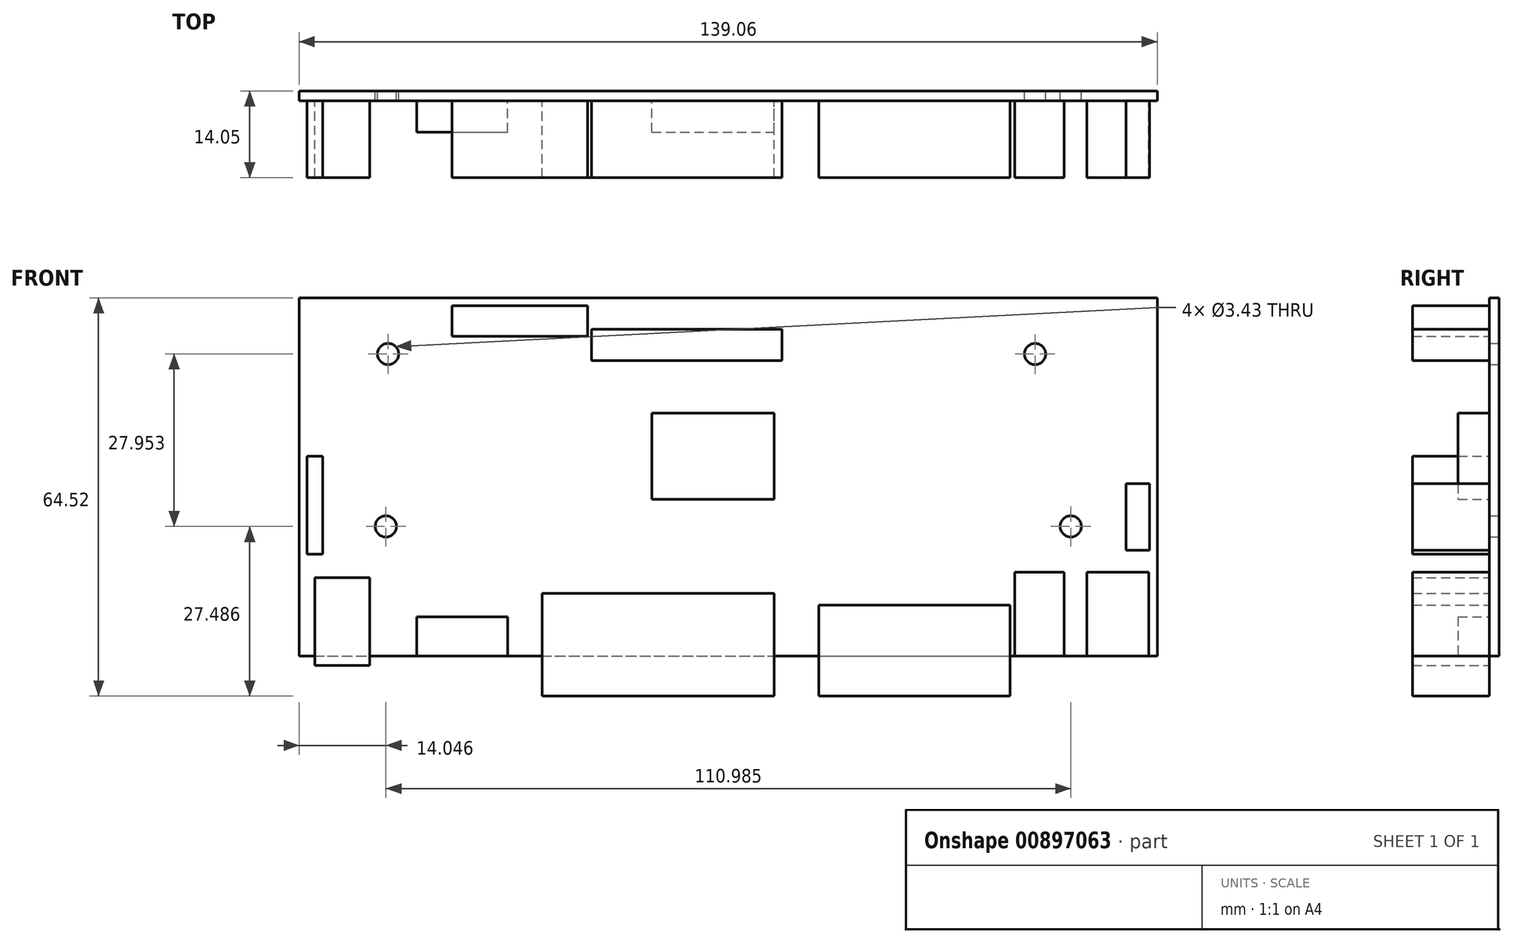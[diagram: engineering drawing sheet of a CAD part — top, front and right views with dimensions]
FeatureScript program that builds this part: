
annotation { "Feature Type Name" : "Feature", "Feature Type Description" : "" }
export const myFeature = defineFeature(function(context is Context, id is Id, definition is map)
    precondition{}
    {
        {
            var Q0;
            Q0=qCreatedBy(makeId("Front.planeOp"),FACE);
            var sketch = newSketch(context, id + "F0", { "sketchPlane" : qUnion([Q0])});
            skLineSegment(sketch, "E0.bottom", {"start": v(0, 0) * mm, "end": v(139.06, 0) * mm});
            skLineSegment(sketch, "E0.top", {"start": v(0, 58.04) * mm, "end": v(139.06, 58.04) * mm});
            skLineSegment(sketch, "E0.left", {"start": v(0, 0) * mm, "end": v(0, 58.04) * mm});
            skLineSegment(sketch, "E0.right", {"start": v(139.06, 0) * mm, "end": v(139.06, 58.04) * mm});
            skCircle(sketch, "E1", {"center": v(14.41, 48.96) * mm, "radius": 1.71 * mm});
            skCircle(sketch, "E2", {"center": v(119.24, 48.95) * mm, "radius": 1.71 * mm});
            skCircle(sketch, "E3", {"center": v(125.03, 21.02) * mm, "radius": 1.71 * mm});
            skCircle(sketch, "E4", {"center": v(14.05, 21) * mm, "radius": 1.71 * mm});
            skSolve(sketch);
        }
        {
            var Q0;
            Q0=makeQuery(id+"F0.imprint","IMPRINT",FACE,{"disambiguationData":[TD([[makeQuery(id+"F0.imprint","IMPRINT",EDGE,{"derivedFrom":sQuery(id+"F0.wireOp",EDGE,"E0.bottom")}),1.0]])]});
            extrude(context, id + "F1", {"entities" : qUnion([Q0]), "depth" : 1.6 * mm, "offsetDistance" : 25.4 * mm});
        }
        {
            var Q0;
            Q0=makeQuery(id+"F1.opExtrude","CAP_FACE",FACE,{"disambiguationData":[OSD([sQuery(id+"F0.wireOp",EDGE,"E0.bottom"),sQuery(id+"F0.wireOp",EDGE,"E0.top"),sQuery(id+"F0.wireOp",EDGE,"E0.left"),sQuery(id+"F0.wireOp",EDGE,"E0.right"),sQuery(id+"F0.wireOp",EDGE,"E1"),sQuery(id+"F0.wireOp",EDGE,"E2"),sQuery(id+"F0.wireOp",EDGE,"E3"),sQuery(id+"F0.wireOp",EDGE,"E4")])],"isStart":false});
            var sketch = newSketch(context, id + "F2", { "sketchPlane" : qUnion([Q0])});
            skLineSegment(sketch, "E5.bottom", {"start": v(2.54, 12.7) * mm, "end": v(11.43, 12.7) * mm});
            skLineSegment(sketch, "E5.top", {"start": v(2.54, -1.52) * mm, "end": v(11.43, -1.52) * mm});
            skLineSegment(sketch, "E5.left", {"start": v(2.54, 12.7) * mm, "end": v(2.54, -1.52) * mm});
            skLineSegment(sketch, "E5.right", {"start": v(11.43, 12.7) * mm, "end": v(11.43, -1.52) * mm});
            skLineSegment(sketch, "E6.bottom", {"start": v(19.05, 6.35) * mm, "end": v(33.78, 6.35) * mm});
            skLineSegment(sketch, "E6.top", {"start": v(19.05, 0) * mm, "end": v(33.78, 0) * mm});
            skLineSegment(sketch, "E6.left", {"start": v(19.05, 6.35) * mm, "end": v(19.05, 0) * mm});
            skLineSegment(sketch, "E6.right", {"start": v(33.78, 6.35) * mm, "end": v(33.78, 0) * mm});
            skLineSegment(sketch, "E7.bottom", {"start": v(39.37, 10.16) * mm, "end": v(76.96, 10.16) * mm});
            skLineSegment(sketch, "E7.top", {"start": v(39.37, 0) * mm, "end": v(76.96, 0) * mm});
            skLineSegment(sketch, "E7.left", {"start": v(39.37, 10.16) * mm, "end": v(39.37, 0) * mm});
            skLineSegment(sketch, "E7.right", {"start": v(76.96, 10.16) * mm, "end": v(76.96, 0) * mm});
            skLineSegment(sketch, "E8.bottom", {"start": v(84.2, 8.26) * mm, "end": v(115.19, 8.26) * mm});
            skLineSegment(sketch, "E8.top", {"start": v(84.2, 0) * mm, "end": v(115.19, 0) * mm});
            skLineSegment(sketch, "E8.left", {"start": v(84.2, 8.26) * mm, "end": v(84.2, 0) * mm});
            skLineSegment(sketch, "E8.right", {"start": v(115.19, 8.26) * mm, "end": v(115.19, 0) * mm});
            skLineSegment(sketch, "E9.bottom", {"start": v(115.95, 0) * mm, "end": v(123.95, 0) * mm});
            skLineSegment(sketch, "E9.top", {"start": v(115.95, 13.59) * mm, "end": v(123.95, 13.59) * mm});
            skLineSegment(sketch, "E9.left", {"start": v(115.95, 0) * mm, "end": v(115.95, 13.59) * mm});
            skLineSegment(sketch, "E9.right", {"start": v(123.95, 0) * mm, "end": v(123.95, 13.59) * mm});
            skLineSegment(sketch, "E10.bottom", {"start": v(127.64, 0) * mm, "end": v(137.67, 0) * mm});
            skLineSegment(sketch, "E10.top", {"start": v(127.64, 13.59) * mm, "end": v(137.67, 13.59) * mm});
            skLineSegment(sketch, "E10.left", {"start": v(127.64, 0) * mm, "end": v(127.64, 13.59) * mm});
            skLineSegment(sketch, "E10.right", {"start": v(137.67, 0) * mm, "end": v(137.67, 13.59) * mm});
            skLineSegment(sketch, "E11.bottom", {"start": v(47.37, 52.96) * mm, "end": v(78.23, 52.96) * mm});
            skLineSegment(sketch, "E11.top", {"start": v(47.37, 47.88) * mm, "end": v(78.23, 47.88) * mm});
            skLineSegment(sketch, "E11.left", {"start": v(47.37, 52.96) * mm, "end": v(47.37, 47.88) * mm});
            skLineSegment(sketch, "E11.right", {"start": v(78.23, 52.96) * mm, "end": v(78.23, 47.88) * mm});
            skLineSegment(sketch, "E12.bottom", {"start": v(46.74, 56.77) * mm, "end": v(24.77, 56.77) * mm});
            skLineSegment(sketch, "E12.top", {"start": v(46.74, 51.82) * mm, "end": v(24.77, 51.82) * mm});
            skLineSegment(sketch, "E12.left", {"start": v(46.74, 56.77) * mm, "end": v(46.74, 51.82) * mm});
            skLineSegment(sketch, "E12.right", {"start": v(24.77, 56.77) * mm, "end": v(24.77, 51.82) * mm});
            skLineSegment(sketch, "E13.bottom", {"start": v(57.15, 39.37) * mm, "end": v(76.96, 39.37) * mm});
            skLineSegment(sketch, "E13.top", {"start": v(57.15, 25.4) * mm, "end": v(76.96, 25.4) * mm});
            skLineSegment(sketch, "E13.left", {"start": v(57.15, 39.37) * mm, "end": v(57.15, 25.4) * mm});
            skLineSegment(sketch, "E13.right", {"start": v(76.96, 39.37) * mm, "end": v(76.96, 25.4) * mm});
            skLineSegment(sketch, "E14.bottom", {"start": v(1.27, 32.39) * mm, "end": v(3.81, 32.39) * mm});
            skLineSegment(sketch, "E14.top", {"start": v(1.27, 16.51) * mm, "end": v(3.81, 16.51) * mm});
            skLineSegment(sketch, "E14.left", {"start": v(1.27, 32.39) * mm, "end": v(1.27, 16.51) * mm});
            skLineSegment(sketch, "E14.right", {"start": v(3.81, 32.39) * mm, "end": v(3.81, 16.51) * mm});
            skLineSegment(sketch, "E15.top", {"start": v(39.37, -6.48) * mm, "end": v(76.96, -6.48) * mm});
            skLineSegment(sketch, "E15.left", {"start": v(39.37, 0) * mm, "end": v(39.37, -6.48) * mm});
            skLineSegment(sketch, "E15.right", {"start": v(76.96, 0) * mm, "end": v(76.96, -6.48) * mm});
            skLineSegment(sketch, "E16.top", {"start": v(84.2, -6.48) * mm, "end": v(115.19, -6.48) * mm});
            skLineSegment(sketch, "E16.left", {"start": v(84.2, 0) * mm, "end": v(84.2, -6.48) * mm});
            skLineSegment(sketch, "E16.right", {"start": v(115.19, 0) * mm, "end": v(115.19, -6.48) * mm});
            skLineSegment(sketch, "E17.bottom", {"start": v(133.98, 27.94) * mm, "end": v(137.8, 27.94) * mm});
            skLineSegment(sketch, "E17.top", {"start": v(133.98, 17.15) * mm, "end": v(137.8, 17.15) * mm});
            skLineSegment(sketch, "E17.left", {"start": v(133.98, 27.94) * mm, "end": v(133.98, 17.15) * mm});
            skLineSegment(sketch, "E17.right", {"start": v(137.8, 27.94) * mm, "end": v(137.8, 17.15) * mm});
            skSolve(sketch);
        }
        {
            var Q0;
            Q0=makeQuery(id+"F2.imprint","IMPRINT",FACE,{"disambiguationData":[TD([[makeQuery(id+"F2.imprint","IMPRINT",EDGE,{"derivedFrom":sQuery(id+"F2.wireOp",EDGE,"E9.bottom")}),1.0]])]});
            var Q1;
            Q1=makeQuery(id+"F2.imprint","IMPRINT",FACE,{"disambiguationData":[TD([[makeQuery(id+"F2.imprint","IMPRINT",EDGE,{"derivedFrom":sQuery(id+"F2.wireOp",EDGE,"E10.bottom")}),1.0]])]});
            var Q2;
            Q2=makeQuery(id+"F2.imprint","IMPRINT",FACE,{"disambiguationData":[TD([[makeQuery(id+"F2.imprint","IMPRINT",EDGE,{"derivedFrom":sQuery(id+"F2.wireOp",EDGE,"E11.bottom")}),-1.0]])]});
            var Q3;
            Q3=makeQuery(id+"F2.imprint","IMPRINT",FACE,{"disambiguationData":[TD([[makeQuery(id+"F2.imprint","IMPRINT",EDGE,{"derivedFrom":sQuery(id+"F2.wireOp",EDGE,"E12.bottom")}),1.0]])]});
            var Q4;
            Q4=makeQuery(id+"F2.imprint","IMPRINT",FACE,{"disambiguationData":[TD([[makeQuery(id+"F2.imprint","IMPRINT",EDGE,{"derivedFrom":sQuery(id+"F2.wireOp",EDGE,"E14.bottom")}),-1.0]])]});
            var Q5;
            Q5=makeQuery(id+"F2.imprint","IMPRINT",FACE,{"disambiguationData":[TD([[makeQuery(id+"F2.imprint","IMPRINT",EDGE,{"derivedFrom":sQuery(id+"F2.wireOp",EDGE,"E7.top")}),-1.0]])]});
            var Q6;
            Q6=makeQuery(id+"F2.imprint","IMPRINT",FACE,{"disambiguationData":[TD([[makeQuery(id+"F2.imprint","IMPRINT",EDGE,{"derivedFrom":sQuery(id+"F2.wireOp",EDGE,"E8.top")}),-1.0]])]});
            var Q7;
            Q7=makeQuery(id+"F2.imprint","IMPRINT",FACE,{"disambiguationData":[TD([[makeQuery(id+"F2.imprint","IMPRINT",EDGE,{"derivedFrom":sQuery(id+"F2.wireOp",EDGE,"E17.bottom")}),-1.0]])]});
            var Q8;
            Q8=makeQuery(id+"F2.imprint","IMPRINT",FACE,{"disambiguationData":[TD([[makeQuery(id+"F2.imprint","IMPRINT",EDGE,{"derivedFrom":sQuery(id+"F2.wireOp",EDGE,"E7.bottom")}),-1.0]])]});
            var Q9;
            Q9=makeQuery(id+"F2.imprint","IMPRINT",FACE,{"disambiguationData":[TD([[makeQuery(id+"F2.imprint","IMPRINT",EDGE,{"derivedFrom":sQuery(id+"F2.wireOp",EDGE,"E8.bottom")}),-1.0]])]});
            var Q10;
            {var subQ0=sQuery(id+"F2.wireOp",EDGE,"E5.top");Q10=makeQuery(id+"F2.imprint","IMPRINT",FACE,{"disambiguationData":[TD([[makeQuery(id+"F2.imprint","IMPRINT",EDGE,{"derivedFrom":subQ0}),1.0]])]});}
            var Q11;
            {var subQ0=sQuery(id+"F2.wireOp",EDGE,"E5.bottom");Q11=makeQuery(id+"F2.imprint","IMPRINT",FACE,{"disambiguationData":[TD([[makeQuery(id+"F2.imprint","IMPRINT",EDGE,{"derivedFrom":subQ0}),-1.0]])]});}
            extrude(context, id + "F3", {"entities" : qUnion([Q0, Q1, Q2, Q3, Q4, Q5, Q6, Q7, Q8, Q9, Q10, Q11]), "operationType" : NewBodyOperationType.ADD, "depth" : 12.45 * mm, "offsetDistance" : 25.4 * mm});
        }
        {
            var Q0;
            Q0=makeQuery(id+"F2.imprint","IMPRINT",FACE,{"disambiguationData":[TD([[makeQuery(id+"F2.imprint","IMPRINT",EDGE,{"derivedFrom":sQuery(id+"F2.wireOp",EDGE,"E13.bottom")}),-1.0]])]});
            var Q1;
            Q1=makeQuery(id+"F2.imprint","IMPRINT",FACE,{"disambiguationData":[TD([[makeQuery(id+"F2.imprint","IMPRINT",EDGE,{"derivedFrom":sQuery(id+"F2.wireOp",EDGE,"E6.bottom")}),-1.0]])]});
            extrude(context, id + "F4", {"entities" : qUnion([Q0, Q1]), "operationType" : NewBodyOperationType.ADD, "depth" : 5.08 * mm, "offsetDistance" : 25.4 * mm});
        }
    });
